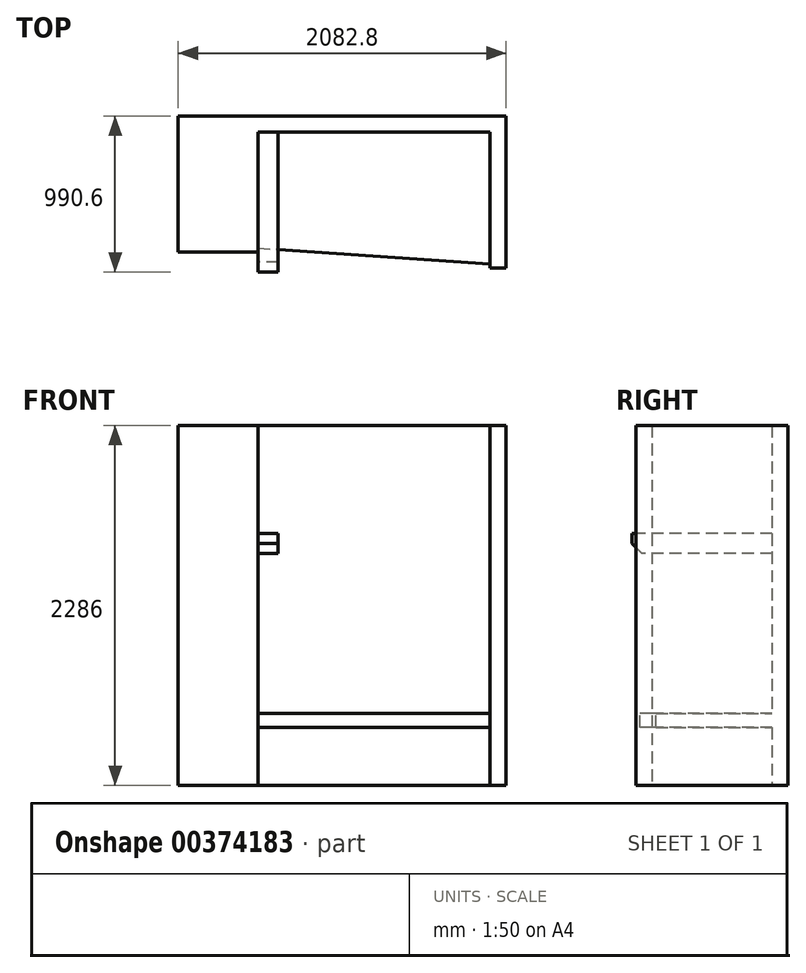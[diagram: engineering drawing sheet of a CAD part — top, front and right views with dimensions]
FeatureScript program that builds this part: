
annotation { "Feature Type Name" : "Feature", "Feature Type Description" : "" }
export const myFeature = defineFeature(function(context is Context, id is Id, definition is map)
    precondition{}
    {
        {
            var Q0;
            Q0=qCreatedBy(makeId("Top.planeOp"),FACE);
            var sketch = newSketch(context, id + "F0", { "sketchPlane" : qUnion([Q0])});
            skLineSegment(sketch, "E0", {"start": v(0, 0) * mm, "end": v(0, 762) * mm});
            skLineSegment(sketch, "E1", {"start": v(0, 762) * mm, "end": v(1473.2, 762) * mm});
            skLineSegment(sketch, "E2", {"start": v(1473.2, 762) * mm, "end": v(1473.2, -101.6) * mm});
            skLineSegment(sketch, "E3", {"start": v(1473.2, -101.6) * mm, "end": v(1574.8, -101.6) * mm});
            skLineSegment(sketch, "E4", {"start": v(1574.8, -101.6) * mm, "end": v(1574.8, 863.6) * mm});
            skLineSegment(sketch, "E5", {"start": v(1574.8, 863.6) * mm, "end": v(-508, 863.6) * mm});
            skLineSegment(sketch, "E6", {"start": v(-508, 863.6) * mm, "end": v(-508, 0) * mm});
            skLineSegment(sketch, "E7", {"start": v(-508, 0) * mm, "end": v(0, 0) * mm});
            skLineSegment(sketch, "E8", {"start": v(0, 25.4) * mm, "end": v(1473.2, -76.2) * mm});
            skSolve(sketch);
        }
        {
            var Q0;
            {var subQ1=sQuery(id+"F0.wireOp",EDGE,"E1");Q0=makeQuery(id+"F0.imprint","IMPRINT",FACE,{"disambiguationData":[TD([[makeQuery(id+"F0.imprint","IMPRINT",EDGE,{"derivedFrom":subQ1}),1.0]])]});}
            extrude(context, id + "F1", {"entities" : qUnion([Q0]), "depth" : 1828.8 * mm, "hasSecondDirection" : true, "secondDirectionOppositeDirection" : true, "secondDirectionDepth" : 457.2 * mm});
        }
        {
            var Q0;
            {var subQ0=sQuery(id+"F0.wireOp",EDGE,"E1");Q0=makeQuery(id+"F0.imprint","IMPRINT",FACE,{"disambiguationData":[TD([[makeQuery(id+"F0.imprint","IMPRINT",EDGE,{"derivedFrom":subQ0}),-1.0]])]});}
            extrude(context, id + "F2", {"entities" : qUnion([Q0]), "operationType" : NewBodyOperationType.ADD, "oppositeDirection" : true, "depth" : 88.9 * mm});
        }
        {
            var Q0;
            Q0=makeQuery(id+"F1.opExtrude","SWEPT_FACE",FACE,{"disambiguationData":[OSD([sQuery(id+"F0.wireOp",EDGE,"E7")])]});
            var sketch = newSketch(context, id + "F3", { "sketchPlane" : qUnion([Q0])});
            skLineSegment(sketch, "E9", {"start": v(0, 1016) * mm, "end": v(127, 1016) * mm});
            skLineSegment(sketch, "E10", {"start": v(127, 1016) * mm, "end": v(127, 1143) * mm});
            skLineSegment(sketch, "E11", {"start": v(127, 1143) * mm, "end": v(0, 1143) * mm});
            skSolve(sketch);
        }
        {
            var Q0;
            {var subQ0=sQuery(id+"F3.wireOp",EDGE,"E9");Q0=makeQuery(id+"F3.imprint","IMPRINT",FACE,{"disambiguationData":[TD([[makeQuery(id+"F3.imprint","IMPRINT",EDGE,{"derivedFrom":subQ0}),1.0]])]});}
            extrude(context, id + "F4", {"entities" : qUnion([Q0]), "endBound" : BoundingType.UP_TO_NEXT, "oppositeDirection" : true, "depth" : 25.4 * mm, "hasSecondDirection" : true, "secondDirectionOppositeDirection" : false, "secondDirectionDepth" : 127 * mm});
        }
        {
            var Q0;
            Q0=makeQuery(id+"F4.opExtrude","CAP_EDGE",EDGE,{"disambiguationData":[OSD([sQuery(id+"F3.wireOp",EDGE,"E9")])],"isStart":true});
            chamfer(context, id + "F5", {"entities" : qUnion([Q0]), "width" : 63.5 * mm, "tangentPropagation" : true});
        }
    });
